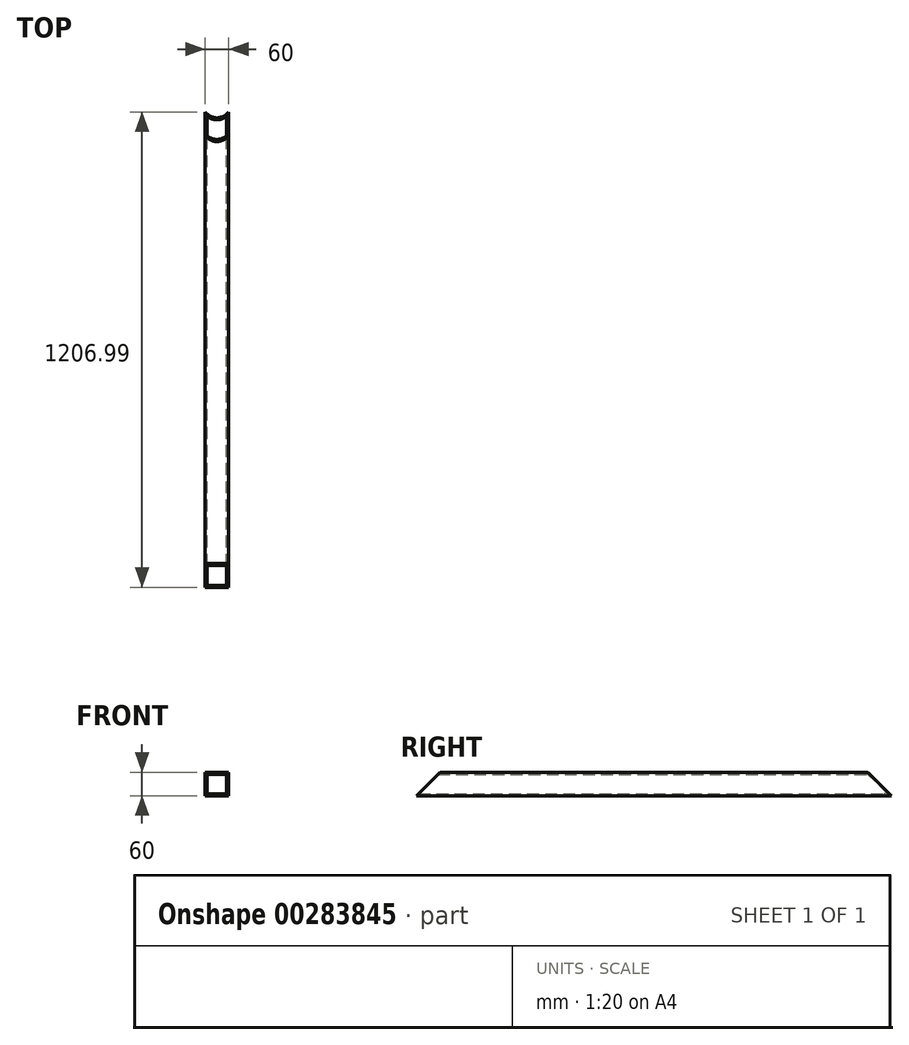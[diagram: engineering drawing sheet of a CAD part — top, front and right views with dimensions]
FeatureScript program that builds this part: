
annotation { "Feature Type Name" : "Feature", "Feature Type Description" : "" }
export const myFeature = defineFeature(function(context is Context, id is Id, definition is map)
    precondition{}
    {
        {
            var Q0;
            Q0=qCreatedBy(makeId("Front.planeOp"),FACE);
            var sketch = newSketch(context, id + "F0", { "sketchPlane" : qUnion([Q0])});
            skLineSegment(sketch, "E0.bottom", {"start": v(-30, -30) * mm, "end": v(30, -30) * mm});
            skLineSegment(sketch, "E0.top", {"start": v(-30, 30) * mm, "end": v(30, 30) * mm});
            skLineSegment(sketch, "E0.left", {"start": v(-30, -30) * mm, "end": v(-30, 30) * mm});
            skLineSegment(sketch, "E0.right", {"start": v(30, -30) * mm, "end": v(30, 30) * mm});
            skPoint(sketch, "E0.middle", {"position": v(0, 0) * mm});
            skLineSegment(sketch, "E1.bottom", {"start": v(25, -25) * mm, "end": v(-25, -25) * mm});
            skLineSegment(sketch, "E1.top", {"start": v(25, 25) * mm, "end": v(-25, 25) * mm});
            skLineSegment(sketch, "E1.left", {"start": v(25, -25) * mm, "end": v(25, 25) * mm});
            skLineSegment(sketch, "E1.right", {"start": v(-25, -25) * mm, "end": v(-25, 25) * mm});
            skSolve(sketch);
        }
        {
            var Q0;
            Q0=makeQuery(id+"F0.imprint","IMPRINT",FACE,{"disambiguationData":[TD([[makeQuery(id+"F0.imprint","IMPRINT",EDGE,{"derivedFrom":sQuery(id+"F0.wireOp",EDGE,"E0.bottom")}),1.0]])]});
            extrude(context, id + "F1", {"entities" : qUnion([Q0]), "depth" : 1207 * mm});
        }
        {
            var Q0;
            Q0=makeQuery(id+"F1.opExtrude","SWEPT_FACE",FACE,{"disambiguationData":[OSD([sQuery(id+"F0.wireOp",EDGE,"E0.right")])]});
            var sketch = newSketch(context, id + "F2", { "sketchPlane" : qUnion([Q0])});
            skLineSegment(sketch, "E2", {"start": v(-1207, -30) * mm, "end": v(-1147, 30) * mm});
            skLineSegment(sketch, "E3", {"start": v(-1147, 30) * mm, "end": v(-1207, 30) * mm});
            skLineSegment(sketch, "E4", {"start": v(-1207, 30) * mm, "end": v(-1207, -30) * mm});
            skLineSegment(sketch, "E5", {"start": v(0, 30) * mm, "end": v(-60, 30) * mm});
            skLineSegment(sketch, "E6", {"start": v(-60, 30) * mm, "end": v(0, -30) * mm});
            skLineSegment(sketch, "E7", {"start": v(0, -30) * mm, "end": v(0, 30) * mm});
            skLineSegment(sketch, "E8", {"start": v(-60, 30) * mm, "end": v(-120, -30) * mm, "construction": true});
            skSolve(sketch);
        }
        {
            var Q0;
            Q0 = qSketchRegion(id + "F2", true);
            extrude(context, id + "F3", {"entities" : qUnion([Q0]), "operationType" : NewBodyOperationType.REMOVE, "endBound" : BoundingType.THROUGH_ALL, "oppositeDirection" : true, "depth" : 25 * mm});
        }
        {
            var Q0;
            Q0=sQuery(id+"F2.wireOp",EDGE,"E8");
            cPlane(context, id + "F4", {"entities" : qUnion([Q0]), "cplaneType" : CPlaneType.LINE_ANGLE, "offset" : 0 * mm, "angle" : 0 * degree, "width" : 150 * mm, "height" : 150 * mm});
        }
        {
            var Q0;
            Q0=qCreatedBy(id+"F4.planeOp",FACE);
            var sketch = newSketch(context, id + "F5", { "sketchPlane" : qUnion([Q0])});
            skCircle(sketch, "E9", {"center": v(0, 17.52) * mm, "radius": 49 * mm});
            skPoint(sketch, "E10", {"position": v(30, -21.21) * mm});
            skSolve(sketch);
        }
        {
            var Q0;
            Q0 = qSketchRegion(id + "F5", true);
            extrude(context, id + "F6", {"entities" : qUnion([Q0]), "operationType" : NewBodyOperationType.REMOVE, "depth" : 236 * mm, "symmetric" : true});
        }
    });
